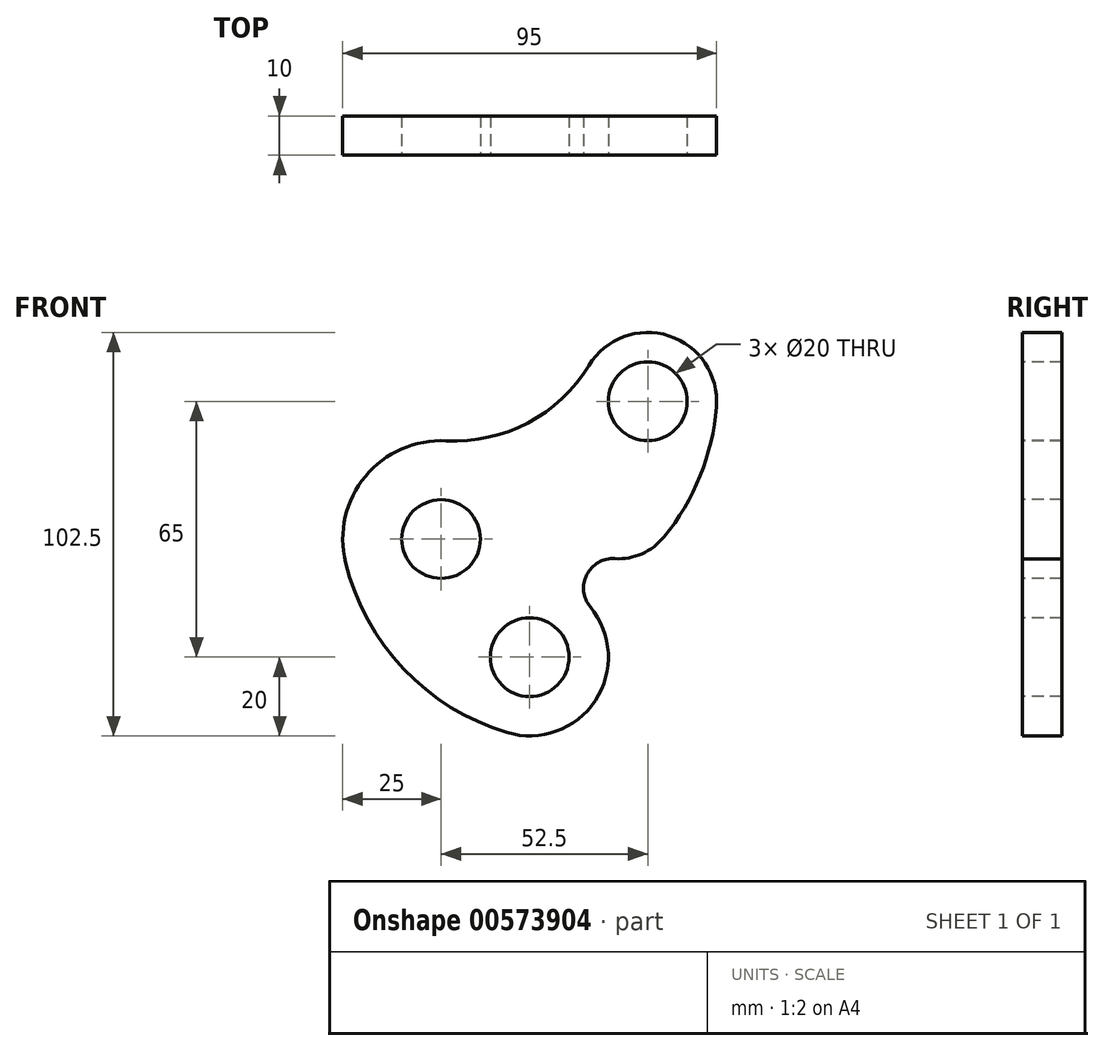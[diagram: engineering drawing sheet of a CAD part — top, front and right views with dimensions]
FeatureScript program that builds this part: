
annotation { "Feature Type Name" : "Feature", "Feature Type Description" : "" }
export const myFeature = defineFeature(function(context is Context, id is Id, definition is map)
    precondition{}
    {
        {
            var Q0;
            Q0=qCreatedBy(makeId("Front.planeOp"),FACE);
            var sketch = newSketch(context, id + "F0", { "sketchPlane" : qUnion([Q0])});
            skCircle(sketch, "E0", {"center": v(0, 0) * mm, "radius": 10 * mm});
            skArc(sketch, "E1", {"start": v(1.3, 24.97) * mm, "mid": v(-19.26, 15.94) * mm, "end": v(-24.28, -5.94) * mm});
            skCircle(sketch, "E2", {"center": v(52.5, 35) * mm, "radius": 10 * mm});
            skArc(sketch, "E3", {"start": v(69.94, 33.58) * mm, "mid": v(57.9, 51.64) * mm, "end": v(37.55, 44.1) * mm});
            skCircle(sketch, "E4", {"center": v(22.5, -30) * mm, "radius": 10 * mm});
            skArc(sketch, "E5", {"start": v(16.75, -49.16) * mm, "mid": v(39.17, -41.05) * mm, "end": v(37.9, -17.24) * mm});
            skArc(sketch, "E6", {"start": v(-24.28, -5.94) * mm, "mid": v(-9.51, -33) * mm, "end": v(16.75, -49.16) * mm});
            skArc(sketch, "E7", {"start": v(1.3, 24.97) * mm, "mid": v(22.07, 29.54) * mm, "end": v(37.55, 44.1) * mm});
            skArc(sketch, "E8", {"start": v(44.12, -4.97) * mm, "mid": v(51.03, -3.73) * mm, "end": v(56.62, 0.51) * mm});
            skArc(sketch, "E9", {"start": v(56.62, 0.51) * mm, "mid": v(65.8, 16.03) * mm, "end": v(69.94, 33.58) * mm});
            skArc(sketch, "E10", {"start": v(44.12, -4.97) * mm, "mid": v(37, -9.07) * mm, "end": v(37.9, -17.24) * mm});
            skSolve(sketch);
        }
        {
            var Q0;
            Q0 = qSketchRegion(id + "F0", true);
            extrude(context, id + "F1", {"entities" : qUnion([Q0]), "oppositeDirection" : true, "depth" : 10 * mm, "offsetDistance" : 25 * mm});
        }
    });
